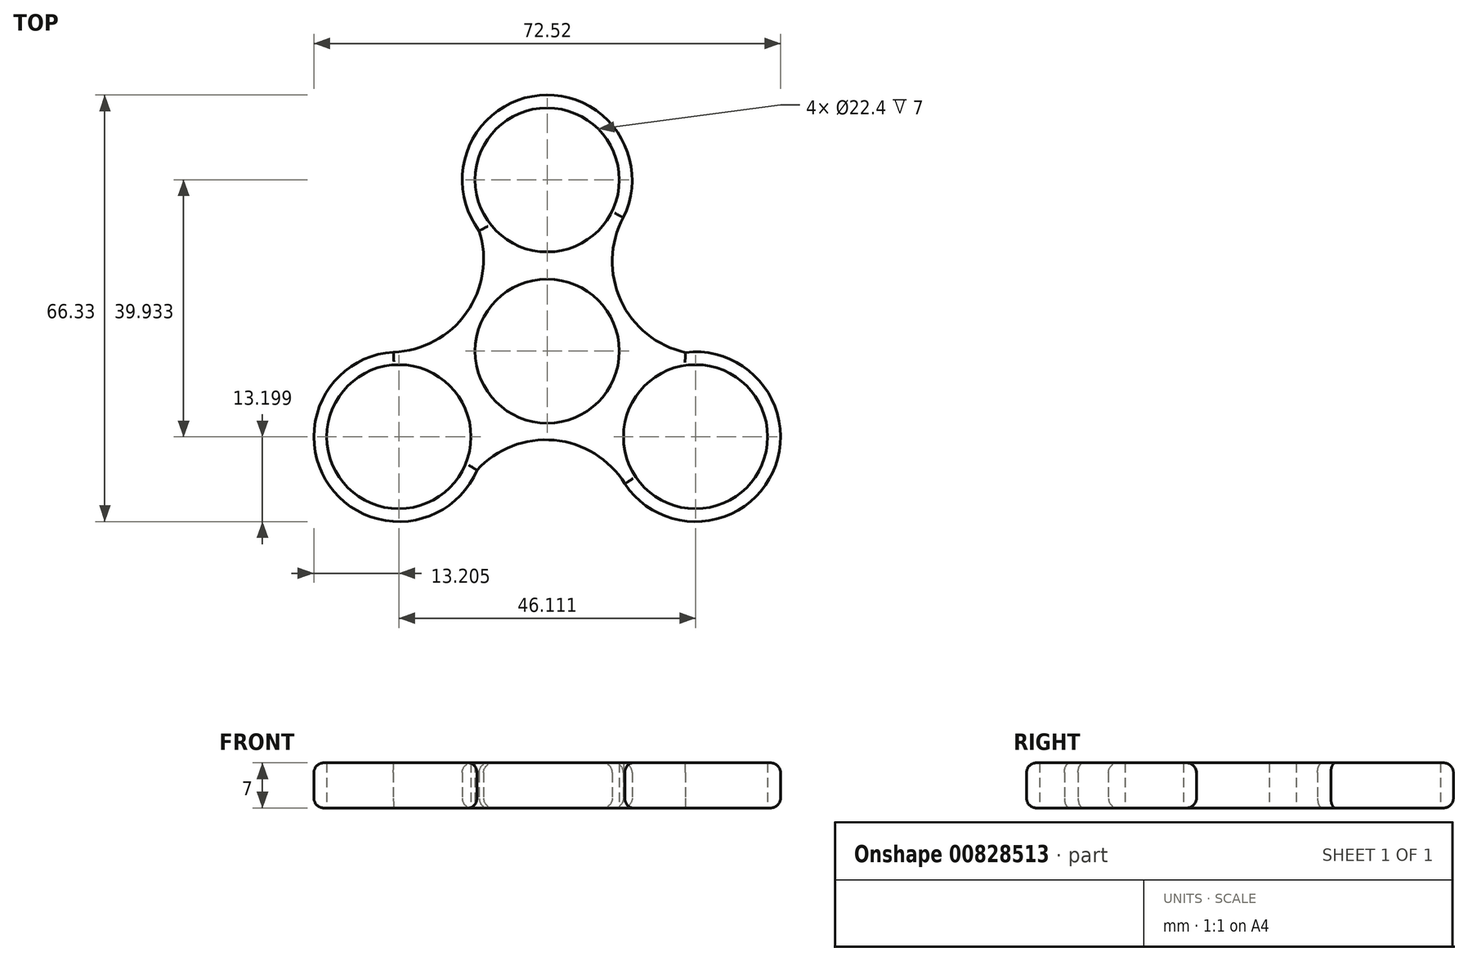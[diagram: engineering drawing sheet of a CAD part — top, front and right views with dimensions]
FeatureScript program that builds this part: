
annotation { "Feature Type Name" : "Feature", "Feature Type Description" : "" }
export const myFeature = defineFeature(function(context is Context, id is Id, definition is map)
    precondition{}
    {
        {
            var Q0;
            Q0=qCreatedBy(makeId("Top.planeOp"),FACE);
            var sketch = newSketch(context, id + "F0", { "sketchPlane" : qUnion([Q0])});
            skCircle(sketch, "E0", {"center": v(0, 0) * mm, "radius": 11.2 * mm});
            skCircle(sketch, "E1", {"center": v(0, 26.62) * mm, "radius": 11.2 * mm});
            skArc(sketch, "E2", {"start": v(11.62, 20.36) * mm, "mid": v(-0.98, 39.79) * mm, "end": v(-10.57, 18.7) * mm});
            skCircle(sketch, "E3.1.0", {"center": v(-23.06, -13.31) * mm, "radius": 11.2 * mm});
            skArc(sketch, "E3.1.1", {"start": v(-23.45, -0.12) * mm, "mid": v(-33.96, -20.74) * mm, "end": v(-10.92, -18.5) * mm});
            skCircle(sketch, "E3.2.0", {"center": v(23.06, -13.31) * mm, "radius": 11.2 * mm});
            skArc(sketch, "E3.2.1", {"start": v(11.83, -20.25) * mm, "mid": v(34.95, -19.04) * mm, "end": v(21.49, -0.2) * mm});
            skLineSegment(sketch, "E4", {"start": v(5.6, 16.92) * mm, "end": v(6.6, 15.2) * mm, "construction": true});
            skLineSegment(sketch, "E5", {"start": v(9.7, 5.6) * mm, "end": v(11.94, 6.9) * mm, "construction": true});
            skArc(sketch, "E6", {"start": v(11.83, 20.77) * mm, "mid": v(11.44, 7.88) * mm, "end": v(21.49, -0.2) * mm});
            skArc(sketch, "E7.1.0", {"start": v(-23.9, -0.14) * mm, "mid": v(-12.54, 5.97) * mm, "end": v(-10.57, 18.7) * mm});
            skArc(sketch, "E7.2.0", {"start": v(12.07, -20.63) * mm, "mid": v(1.1, -13.85) * mm, "end": v(-10.92, -18.5) * mm});
            skLineSegment(sketch, "E8.trimOffspring", {"start": v(16.46, -1.88) * mm, "end": v(17.46, -3.61) * mm, "construction": true});
            skSolve(sketch);
        }
        {
            var Q0;
            Q0=makeQuery(id+"F0.imprint","IMPRINT",FACE,{"disambiguationData":[TD([[makeQuery(id+"F0.imprint","IMPRINT",EDGE,{"derivedFrom":sQuery(id+"F0.wireOp",EDGE,"E0")}),-1.0]])]});
            extrude(context, id + "F1", {"entities" : qUnion([Q0]), "depth" : 7 * mm, "offsetDistance" : 25 * mm});
        }
        {
            var Q0;
            Q0=makeQuery(id+"F1.opExtrude","CAP_EDGE",EDGE,{"disambiguationData":[OSD([sQuery(id+"F0.wireOp",EDGE,"E3.1.1")])],"isStart":false});
            var Q1;
            Q1=makeQuery(id+"F1.opExtrude","CAP_EDGE",EDGE,{"disambiguationData":[OSD([sQuery(id+"F0.wireOp",EDGE,"E7.2.0")])],"isStart":false});
            var Q2;
            Q2=makeQuery(id+"F1.opExtrude","CAP_EDGE",EDGE,{"disambiguationData":[OSD([sQuery(id+"F0.wireOp",EDGE,"E3.2.1")])],"isStart":false});
            var Q3;
            Q3=makeQuery(id+"F1.opExtrude","CAP_EDGE",EDGE,{"disambiguationData":[OSD([sQuery(id+"F0.wireOp",EDGE,"E6")])],"isStart":false});
            var Q4;
            Q4=makeQuery(id+"F1.opExtrude","CAP_EDGE",EDGE,{"disambiguationData":[OSD([sQuery(id+"F0.wireOp",EDGE,"E2")])],"isStart":false});
            var Q5;
            Q5=makeQuery(id+"F1.opExtrude","CAP_EDGE",EDGE,{"disambiguationData":[OSD([sQuery(id+"F0.wireOp",EDGE,"E7.1.0")])],"isStart":false});
            fillet(context, id + "F2", {"entities" : qUnion([Q0, Q1, Q2, Q3, Q4, Q5]), "radius" : 1.5 * mm, "tangentPropagation" : true, "allowEdgeOverflow" : false});
        }
        {
            var Q0;
            Q0=makeQuery(id+"F1.opExtrude","CAP_EDGE",EDGE,{"disambiguationData":[OSD([sQuery(id+"F0.wireOp",EDGE,"E3.1.1")])],"isStart":true});
            var Q1;
            Q1=makeQuery(id+"F1.opExtrude","CAP_EDGE",EDGE,{"disambiguationData":[OSD([sQuery(id+"F0.wireOp",EDGE,"E7.1.0")])],"isStart":true});
            var Q2;
            Q2=makeQuery(id+"F1.opExtrude","CAP_EDGE",EDGE,{"disambiguationData":[OSD([sQuery(id+"F0.wireOp",EDGE,"E2")])],"isStart":true});
            var Q3;
            Q3=makeQuery(id+"F1.opExtrude","CAP_EDGE",EDGE,{"disambiguationData":[OSD([sQuery(id+"F0.wireOp",EDGE,"E6")])],"isStart":true});
            var Q4;
            Q4=makeQuery(id+"F1.opExtrude","CAP_EDGE",EDGE,{"disambiguationData":[OSD([sQuery(id+"F0.wireOp",EDGE,"E3.2.1")])],"isStart":true});
            var Q5;
            Q5=makeQuery(id+"F1.opExtrude","CAP_EDGE",EDGE,{"disambiguationData":[OSD([sQuery(id+"F0.wireOp",EDGE,"E7.2.0")])],"isStart":true});
            fillet(context, id + "F3", {"entities" : qUnion([Q0, Q1, Q2, Q3, Q4, Q5]), "radius" : 1.5 * mm, "tangentPropagation" : true, "allowEdgeOverflow" : false});
        }
    });
